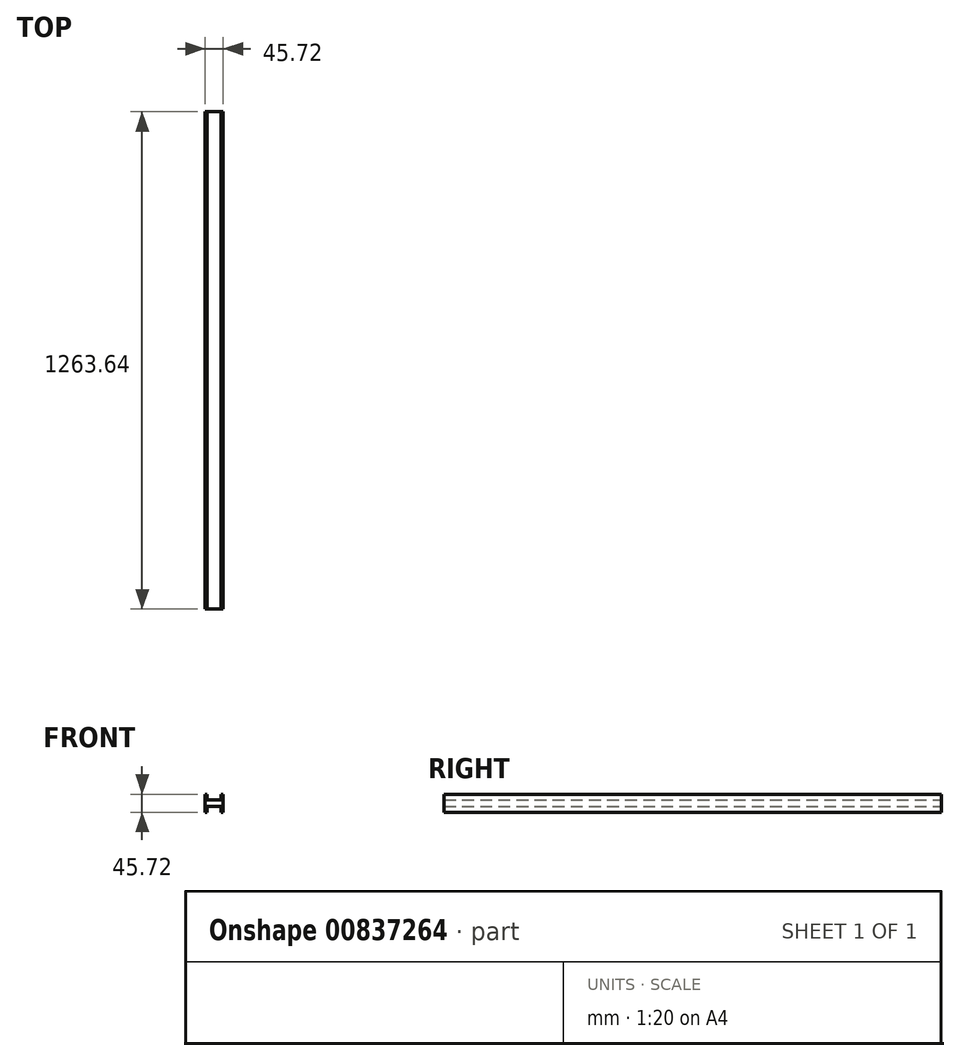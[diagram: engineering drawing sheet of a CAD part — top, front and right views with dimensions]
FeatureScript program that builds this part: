
annotation { "Feature Type Name" : "Feature", "Feature Type Description" : "" }
export const myFeature = defineFeature(function(context is Context, id is Id, definition is map)
    precondition{}
    {
        {
            var Q0;
            Q0=qCreatedBy(makeId("Front.planeOp"),FACE);
            var sketch = newSketch(context, id + "F0", { "sketchPlane" : qUnion([Q0])});
            skLineSegment(sketch, "E0.bottom", {"start": v(22.86, 22.86) * mm, "end": v(17.8, 22.86) * mm});
            skLineSegment(sketch, "E0.top", {"start": v(22.86, -22.86) * mm, "end": v(17.8, -22.86) * mm});
            skLineSegment(sketch, "E0.left", {"start": v(22.86, 22.86) * mm, "end": v(22.86, -22.86) * mm});
            skLineSegment(sketch, "E0.right", {"start": v(-22.86, 22.86) * mm, "end": v(-22.86, -22.86) * mm});
            skPoint(sketch, "E0.middle", {"position": v(0, 0) * mm});
            skLineSegment(sketch, "E1.top", {"start": v(-18.22, 8.64) * mm, "end": v(17.8, 8.64) * mm});
            skLineSegment(sketch, "E1.left", {"start": v(-18.22, 22.86) * mm, "end": v(-18.22, 8.64) * mm});
            skLineSegment(sketch, "E1.right", {"start": v(17.8, 22.86) * mm, "end": v(17.8, 8.64) * mm});
            skLineSegment(sketch, "E2", {"start": v(-65.42, 0) * mm, "end": v(65.2, 0) * mm, "construction": true});
            skLineSegment(sketch, "E3.MirrorCS", {"start": v(-18.22, -22.86) * mm, "end": v(-18.22, -8.64) * mm});
            skLineSegment(sketch, "E4.MirrorCS", {"start": v(-18.22, -8.64) * mm, "end": v(17.8, -8.64) * mm});
            skLineSegment(sketch, "E5.MirrorCS", {"start": v(17.8, -22.86) * mm, "end": v(17.8, -8.64) * mm});
            skLineSegment(sketch, "E6.trimOffspring", {"start": v(-18.22, 22.86) * mm, "end": v(-22.86, 22.86) * mm});
            skPoint(sketch, "E7.orphan", {"position": v(17.8, -31.29) * mm});
            skLineSegment(sketch, "E8.trimOffspring", {"start": v(-18.22, -22.86) * mm, "end": v(-22.86, -22.86) * mm});
            skPoint(sketch, "E9.orphan", {"position": v(-18.22, -31.29) * mm});
            skSolve(sketch);
        }
        {
            var Q0;
            Q0=qSketchRegion(id+"F0",true);
            extrude(context, id + "F1", {"entities" : qUnion([Q0]), "endBound" : BoundingType.SYMMETRIC, "depth" : 1263.65 * mm, "offsetDistance" : 25.4 * mm});
        }
    });
